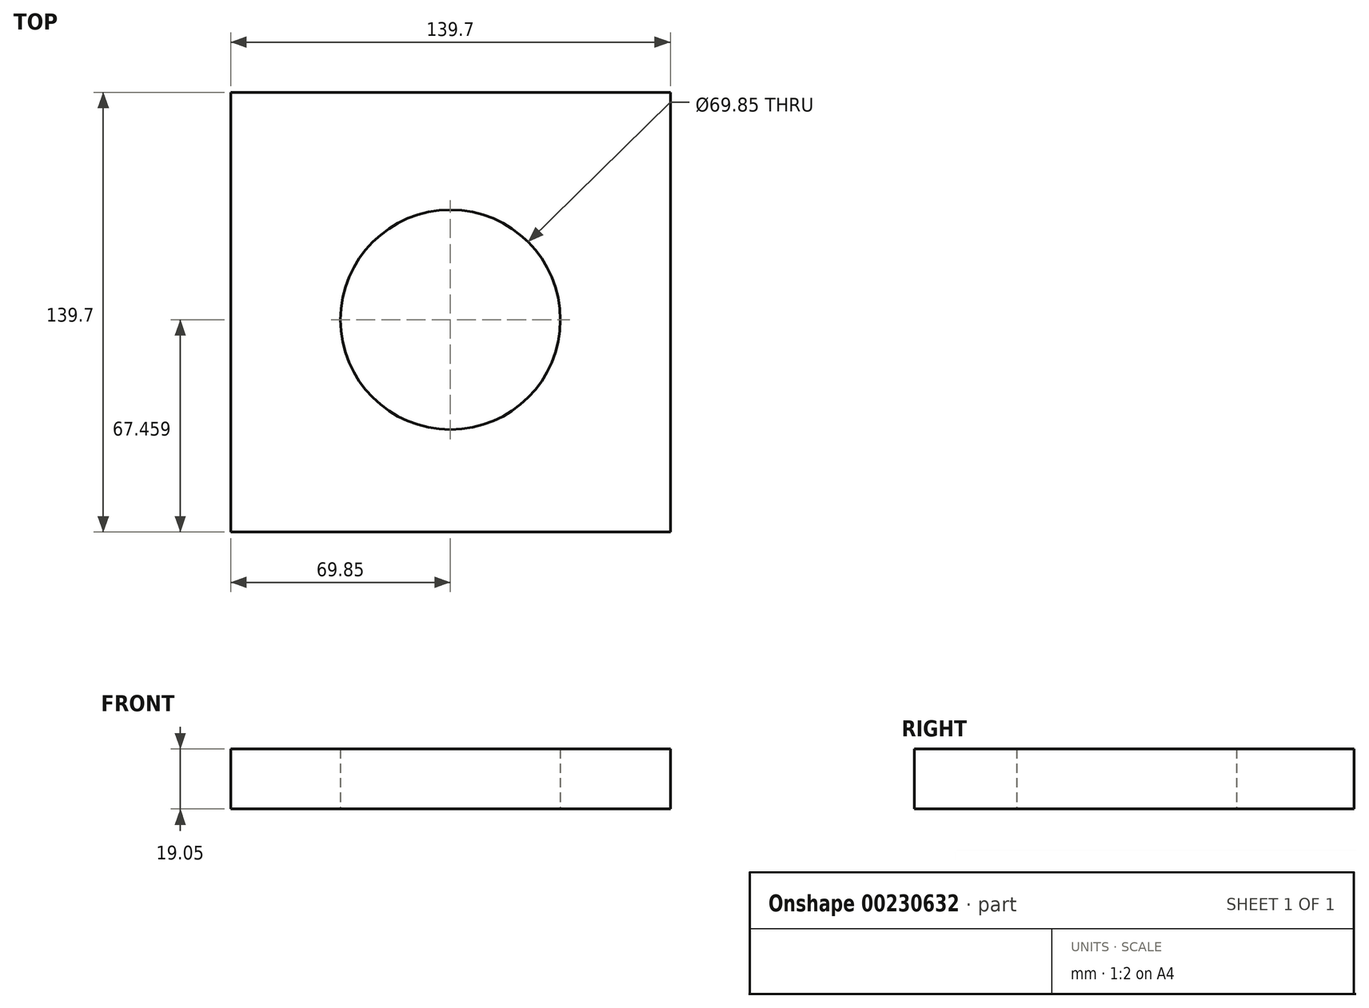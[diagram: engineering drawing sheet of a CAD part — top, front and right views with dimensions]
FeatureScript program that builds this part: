
annotation { "Feature Type Name" : "Feature", "Feature Type Description" : "" }
export const myFeature = defineFeature(function(context is Context, id is Id, definition is map)
    precondition{}
    {
        {
            var Q0;
            Q0=qCreatedBy(makeId("Top.planeOp"),FACE);
            var sketch = newSketch(context, id + "F0", { "sketchPlane" : qUnion([Q0])});
            skLineSegment(sketch, "E0.bottom", {"start": v(-69.85, 69.85) * mm, "end": v(69.85, 69.85) * mm});
            skLineSegment(sketch, "E0.top", {"start": v(-69.85, -69.85) * mm, "end": v(69.85, -69.85) * mm});
            skLineSegment(sketch, "E0.left", {"start": v(-69.85, 69.85) * mm, "end": v(-69.85, -69.85) * mm});
            skLineSegment(sketch, "E0.right", {"start": v(69.85, 69.85) * mm, "end": v(69.85, -69.85) * mm});
            skPoint(sketch, "E0.middle", {"position": v(0, 0) * mm});
            skCircle(sketch, "E1", {"center": v(0, -2.4) * mm, "radius": 34.93 * mm});
            skSolve(sketch);
        }
        {
            var Q0;
            Q0 = qSketchRegion(id + "F0", true);
            extrude(context, id + "F1", {"entities" : qUnion([Q0]), "depth" : 19.05 * mm});
        }
    });
